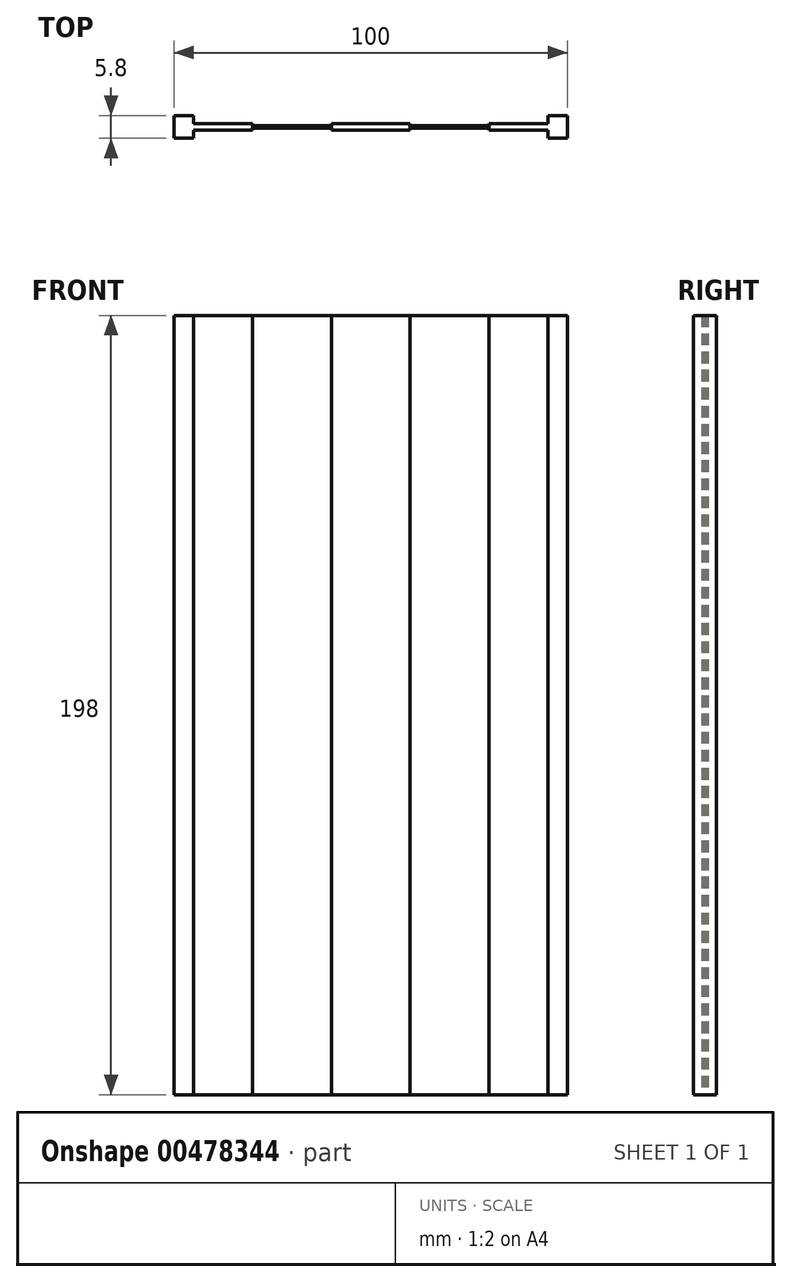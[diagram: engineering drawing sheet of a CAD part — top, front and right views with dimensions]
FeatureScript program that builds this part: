
annotation { "Feature Type Name" : "Feature", "Feature Type Description" : "" }
export const myFeature = defineFeature(function(context is Context, id is Id, definition is map)
    precondition{}
    {
        {
            var Q0;
            Q0=qCreatedBy(makeId("Front.planeOp"),FACE);
            var sketch = newSketch(context, id + "F0", { "sketchPlane" : qUnion([Q0])});
            skLineSegment(sketch, "E0.bottom", {"start": v(50, -99) * mm, "end": v(-50, -99) * mm});
            skLineSegment(sketch, "E0.top", {"start": v(50, 99) * mm, "end": v(-50, 99) * mm});
            skLineSegment(sketch, "E0.left", {"start": v(50, -99) * mm, "end": v(50, 99) * mm});
            skLineSegment(sketch, "E0.right", {"start": v(-50, -99) * mm, "end": v(-50, 99) * mm});
            skPoint(sketch, "E0.middle", {"position": v(0, 0) * mm});
            skLineSegment(sketch, "E1", {"start": v(45, 99) * mm, "end": v(45, -99) * mm});
            skLineSegment(sketch, "E2", {"start": v(30, 99) * mm, "end": v(30, -99) * mm});
            skLineSegment(sketch, "E3", {"start": v(10, 99) * mm, "end": v(10, -99) * mm});
            skLineSegment(sketch, "E4", {"start": v(-10, 99) * mm, "end": v(-10, -99) * mm});
            skLineSegment(sketch, "E5", {"start": v(-30, 99) * mm, "end": v(-30, -99) * mm});
            skLineSegment(sketch, "E6", {"start": v(-45, 99) * mm, "end": v(-45, -99) * mm});
            skSolve(sketch);
        }
        {
            var Q0;
            {var subQ0=sQuery(id+"F0.wireOp",EDGE,"E0.left");Q0=makeQuery(id+"F0.imprint","IMPRINT",FACE,{"disambiguationData":[TD([[makeQuery(id+"F0.imprint","IMPRINT",EDGE,{"derivedFrom":subQ0}),1.0]])]});}
            var Q1;
            {var subQ0=sQuery(id+"F0.wireOp",EDGE,"E0.right");Q1=makeQuery(id+"F0.imprint","IMPRINT",FACE,{"disambiguationData":[TD([[makeQuery(id+"F0.imprint","IMPRINT",EDGE,{"derivedFrom":subQ0}),-1.0]])]});}
            extrude(context, id + "F1", {"entities" : qUnion([Q0, Q1]), "endBound" : BoundingType.SYMMETRIC, "depth" : 5.8 * mm, "offsetDistance" : 25 * mm});
        }
        {
            var Q0;
            {var subQ0=sQuery(id+"F0.wireOp",EDGE,"E1");Q0=makeQuery(id+"F0.imprint","IMPRINT",FACE,{"disambiguationData":[TD([[makeQuery(id+"F0.imprint","IMPRINT",EDGE,{"derivedFrom":subQ0}),-1.0]])]});}
            var Q1;
            {var subQ0=sQuery(id+"F0.wireOp",EDGE,"E3");Q1=makeQuery(id+"F0.imprint","IMPRINT",FACE,{"disambiguationData":[TD([[makeQuery(id+"F0.imprint","IMPRINT",EDGE,{"derivedFrom":subQ0}),-1.0]])]});}
            var Q2;
            {var subQ0=sQuery(id+"F0.wireOp",EDGE,"E0.right");Q2=makeQuery(id+"F0.imprint","IMPRINT",FACE,{"disambiguationData":[TD([[makeQuery(id+"F0.imprint","IMPRINT",EDGE,{"derivedFrom":subQ0}),-1.0]])]});}
            var Q3;
            {var subQ0=sQuery(id+"F0.wireOp",EDGE,"E5");Q3=makeQuery(id+"F0.imprint","IMPRINT",FACE,{"disambiguationData":[TD([[makeQuery(id+"F0.imprint","IMPRINT",EDGE,{"derivedFrom":subQ0}),-1.0]])]});}
            extrude(context, id + "F2", {"entities" : qUnion([Q0, Q1, Q2, Q3]), "operationType" : NewBodyOperationType.ADD, "endBound" : BoundingType.SYMMETRIC, "depth" : 1.6 * mm, "offsetDistance" : 25 * mm});
        }
        {
            var Q0;
            {var subQ0=sQuery(id+"F0.wireOp",EDGE,"E4");Q0=makeQuery(id+"F0.imprint","IMPRINT",FACE,{"disambiguationData":[TD([[makeQuery(id+"F0.imprint","IMPRINT",EDGE,{"derivedFrom":subQ0}),-1.0]])]});}
            var Q1;
            {var subQ0=sQuery(id+"F0.wireOp",EDGE,"E2");Q1=makeQuery(id+"F0.imprint","IMPRINT",FACE,{"disambiguationData":[TD([[makeQuery(id+"F0.imprint","IMPRINT",EDGE,{"derivedFrom":subQ0}),-1.0]])]});}
            extrude(context, id + "F3", {"entities" : qUnion([Q0, Q1]), "endBound" : BoundingType.SYMMETRIC, "depth" : 0.6 * mm, "offsetDistance" : 25 * mm});
        }
    });
